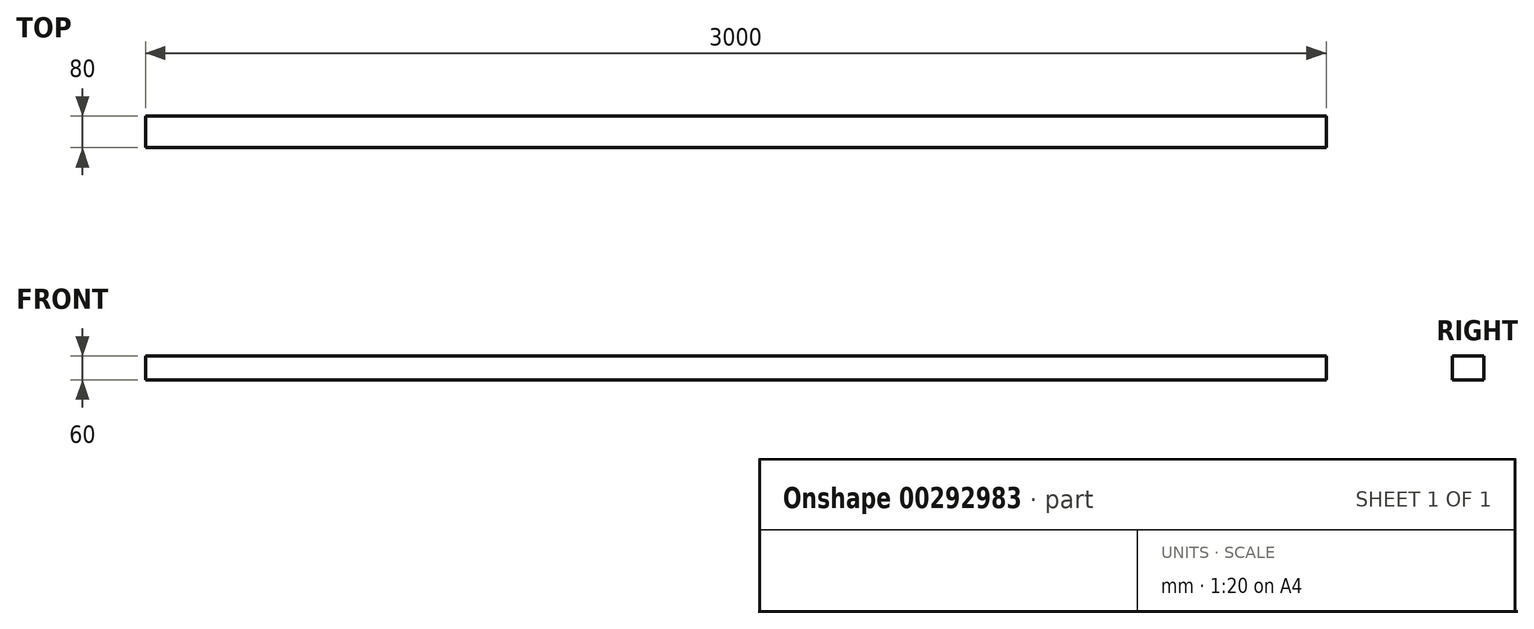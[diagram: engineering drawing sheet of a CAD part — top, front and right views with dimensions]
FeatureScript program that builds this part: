
annotation { "Feature Type Name" : "Feature", "Feature Type Description" : "" }
export const myFeature = defineFeature(function(context is Context, id is Id, definition is map)
    precondition{}
    {
        {
            var Q0;
            Q0=qCreatedBy(makeId("Right.planeOp"),FACE);
            var sketch = newSketch(context, id + "F0", { "sketchPlane" : qUnion([Q0])});
            skLineSegment(sketch, "E0.bottom", {"start": v(-7.5, 54.81) * mm, "end": v(72.5, 54.81) * mm});
            skLineSegment(sketch, "E0.top", {"start": v(-7.5, -5.19) * mm, "end": v(72.5, -5.19) * mm});
            skLineSegment(sketch, "E0.left", {"start": v(-7.5, 54.81) * mm, "end": v(-7.5, -5.19) * mm});
            skLineSegment(sketch, "E0.right", {"start": v(72.5, 54.81) * mm, "end": v(72.5, -5.19) * mm});
            skSolve(sketch);
        }
        {
            var Q0;
            Q0=makeQuery(id+"F0.imprint","IMPRINT",FACE,{"disambiguationData":[TD([[makeQuery(id+"F0.imprint","IMPRINT",EDGE,{"derivedFrom":sQuery(id+"F0.wireOp",EDGE,"E0.bottom")}),-1.0]])]});
            extrude(context, id + "F1", {"entities" : qUnion([Q0]), "depth" : 3000 * mm});
        }
    });
